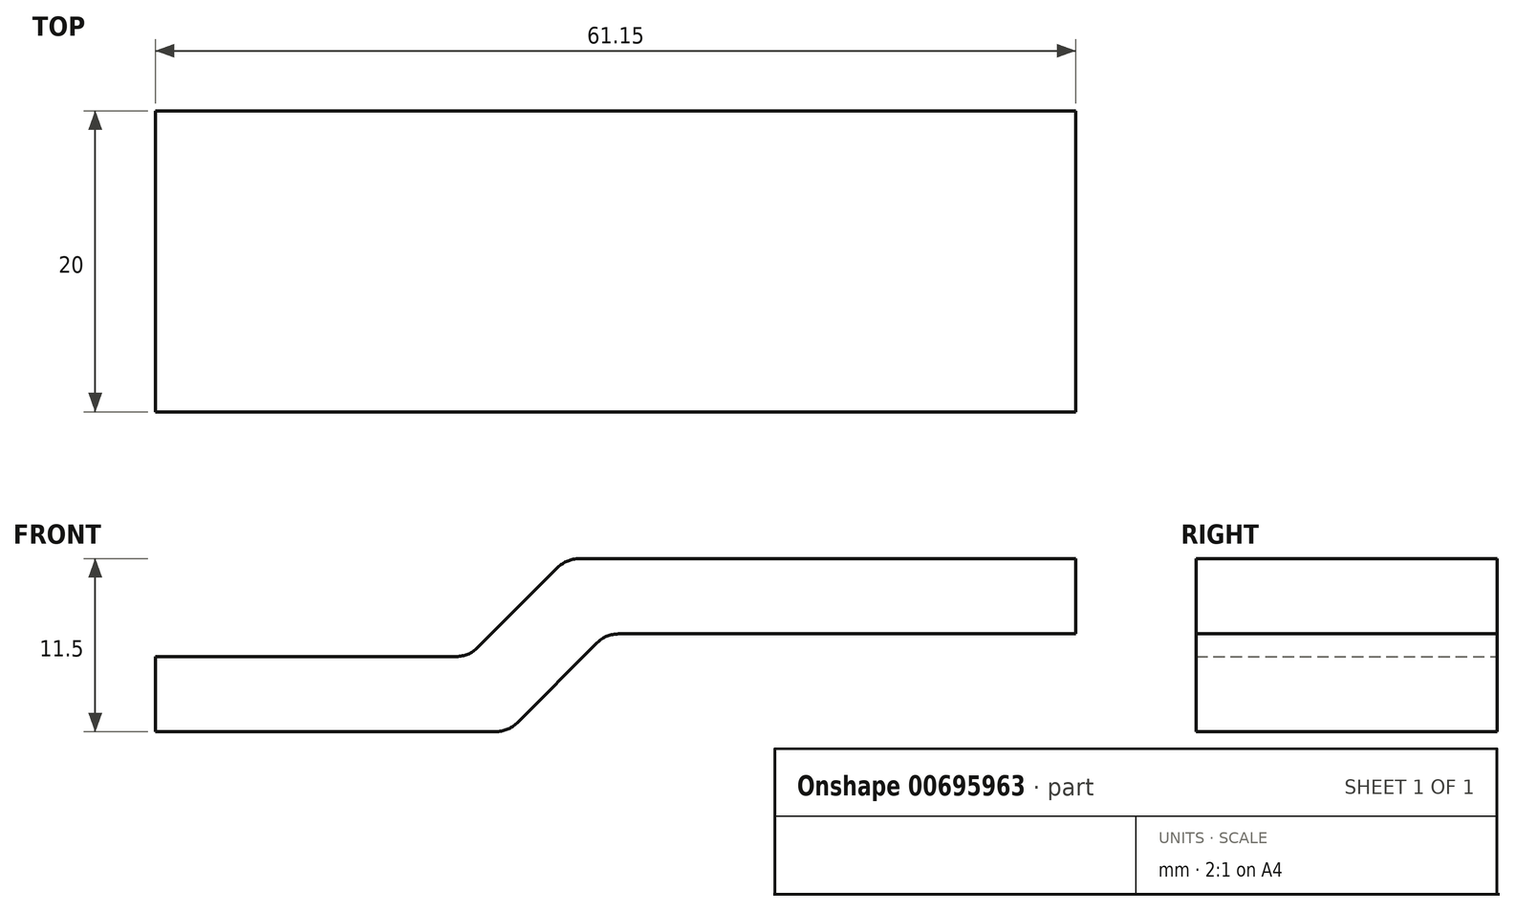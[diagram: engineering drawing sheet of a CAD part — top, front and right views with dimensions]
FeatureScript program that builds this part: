
annotation { "Feature Type Name" : "Feature", "Feature Type Description" : "" }
export const myFeature = defineFeature(function(context is Context, id is Id, definition is map)
    precondition{}
    {
        {
            var Q0;
            Q0=qCreatedBy(makeId("Front.planeOp"),FACE);
            var sketch = newSketch(context, id + "F0", { "sketchPlane" : qUnion([Q0])});
            skLineSegment(sketch, "E0", {"start": v(-29.92, 8) * mm, "end": v(-9.92, 8) * mm});
            skLineSegment(sketch, "E1", {"start": v(-8.5, 8.6) * mm, "end": v(-3.18, 13.92) * mm});
            skLineSegment(sketch, "E2", {"start": v(-1.77, 14.5) * mm, "end": v(31.23, 14.5) * mm});
            skPoint(sketch, "E3.end.orphan", {"position": v(-29.92, 3) * mm});
            skPoint(sketch, "E4.visualSharp", {"position": v(-2.6, 14.5) * mm});
            skArc(sketch, "E4.filletArc", {"start": v(-1.77, 14.5) * mm, "mid": v(-2.53, 14.36) * mm, "end": v(-3.18, 13.92) * mm});
            skPoint(sketch, "E5.visualSharp", {"position": v(-9.1, 8) * mm});
            skArc(sketch, "E5.filletArc", {"start": v(-9.92, 8) * mm, "mid": v(-9.16, 8.16) * mm, "end": v(-8.5, 8.6) * mm});
            skLineSegment(sketch, "E6", {"start": v(-29.92, 8) * mm, "end": v(-29.92, 3) * mm});
            skLineSegment(sketch, "E7", {"start": v(-29.92, 3) * mm, "end": v(-7.32, 3) * mm});
            skLineSegment(sketch, "E8", {"start": v(-5.9, 3.6) * mm, "end": v(-0.57, 8.92) * mm});
            skLineSegment(sketch, "E9", {"start": v(0.84, 9.5) * mm, "end": v(31.23, 9.5) * mm});
            skLineSegment(sketch, "E10", {"start": v(31.23, 9.5) * mm, "end": v(31.23, 14.5) * mm});
            skPoint(sketch, "E11.visualSharp", {"position": v(-6.49, 3) * mm});
            skArc(sketch, "E11.filletArc", {"start": v(-7.32, 3) * mm, "mid": v(-6.55, 3.16) * mm, "end": v(-5.9, 3.6) * mm});
            skPoint(sketch, "E12.visualSharp", {"position": v(0.01, 9.5) * mm});
            skArc(sketch, "E12.filletArc", {"start": v(0.84, 9.5) * mm, "mid": v(0.07, 9.36) * mm, "end": v(-0.57, 8.92) * mm});
            skSolve(sketch);
        }
        {
            var Q0;
            Q0=makeQuery(id+"F0.imprint","IMPRINT",FACE,{"disambiguationData":[TD([[makeQuery(id+"F0.imprint","IMPRINT",EDGE,{"derivedFrom":sQuery(id+"F0.wireOp",EDGE,"E0")}),-1.0]])]});
            extrude(context, id + "F1", {"entities" : qUnion([Q0]), "depth" : 20 * mm, "offsetDistance" : 25 * mm});
        }
    });
